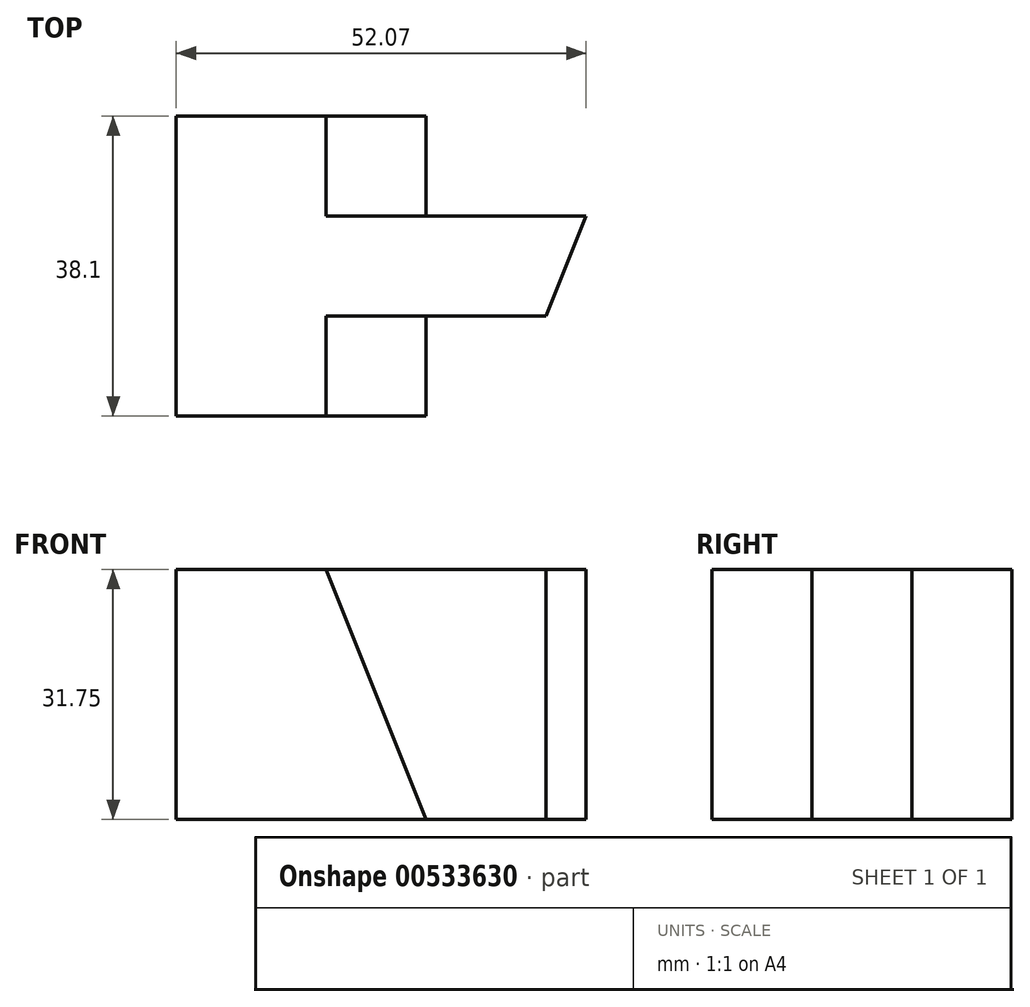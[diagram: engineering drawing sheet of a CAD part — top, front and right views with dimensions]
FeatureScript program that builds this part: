
annotation { "Feature Type Name" : "Feature", "Feature Type Description" : "" }
export const myFeature = defineFeature(function(context is Context, id is Id, definition is map)
    precondition{}
    {
        {
            var Q0;
            Q0=qCreatedBy(makeId("Front.planeOp"),FACE);
            var sketch = newSketch(context, id + "F0", { "sketchPlane" : qUnion([Q0])});
            skLineSegment(sketch, "E0", {"start": v(-43.55, 31.75) * mm, "end": v(-43.55, 0) * mm});
            skLineSegment(sketch, "E1", {"start": v(-43.55, 31.75) * mm, "end": v(-11.8, 31.75) * mm});
            skLineSegment(sketch, "E2", {"start": v(-11.8, 31.75) * mm, "end": v(-11.8, 0) * mm});
            skLineSegment(sketch, "E3", {"start": v(-11.8, 0) * mm, "end": v(-43.55, 0) * mm});
            skSolve(sketch);
        }
        {
            var Q0;
            Q0=makeQuery(id+"F0.imprint","IMPRINT",FACE,{"disambiguationData":[TD([[makeQuery(id+"F0.imprint","IMPRINT",EDGE,{"derivedFrom":sQuery(id+"F0.wireOp",EDGE,"E0")}),1.0]])]});
            extrude(context, id + "F1", {"entities" : qUnion([Q0]), "depth" : 38.1 * mm, "offsetDistance" : 25.4 * mm});
        }
        {
            var Q0;
            Q0=makeQuery(id+"F1.opExtrude","CAP_FACE",FACE,{"disambiguationData":[OSD([sQuery(id+"F0.wireOp",EDGE,"E0"),sQuery(id+"F0.wireOp",EDGE,"E1"),sQuery(id+"F0.wireOp",EDGE,"E2"),sQuery(id+"F0.wireOp",EDGE,"E3")])],"isStart":false});
            var sketch = newSketch(context, id + "F2", { "sketchPlane" : qUnion([Q0])});
            skLineSegment(sketch, "E4", {"start": v(-24.5, 31.75) * mm, "end": v(-11.8, 0) * mm});
            skSolve(sketch);
        }
        {
            var Q0;
            {var subQ0=sQuery(id+"F2.wireOp",EDGE,"E4");Q0=makeQuery(id+"F2.imprint","IMPRINT",FACE,{"disambiguationData":[TD([[makeQuery(id+"F2.imprint","IMPRINT",EDGE,{"derivedFrom":subQ0}),1.0]])]});}
            extrude(context, id + "F3", {"entities" : qUnion([Q0]), "operationType" : NewBodyOperationType.REMOVE, "oppositeDirection" : true, "depth" : 12.7 * mm, "offsetDistance" : 25.4 * mm});
        }
        {
            var Q0;
            Q0=makeQuery(id+"F1.opExtrude","CAP_FACE",FACE,{"disambiguationData":[OSD([sQuery(id+"F0.wireOp",EDGE,"E0"),sQuery(id+"F0.wireOp",EDGE,"E1"),sQuery(id+"F0.wireOp",EDGE,"E2"),sQuery(id+"F0.wireOp",EDGE,"E3")])],"isStart":true});
            var sketch = newSketch(context, id + "F4", { "sketchPlane" : qUnion([Q0])});
            skLineSegment(sketch, "E5", {"start": v(24.5, 31.75) * mm, "end": v(11.8, 0) * mm});
            skSolve(sketch);
        }
        {
            var Q0;
            {var subQ0=sQuery(id+"F4.wireOp",EDGE,"E5");Q0=makeQuery(id+"F4.imprint","IMPRINT",FACE,{"disambiguationData":[TD([[makeQuery(id+"F4.imprint","IMPRINT",EDGE,{"derivedFrom":subQ0}),-1.0]])]});}
            extrude(context, id + "F5", {"entities" : qUnion([Q0]), "operationType" : NewBodyOperationType.REMOVE, "oppositeDirection" : true, "depth" : 12.7 * mm, "offsetDistance" : 25.4 * mm});
        }
        {
            var Q0;
            Q0=makeQuery(id+"F1.opExtrude","SWEPT_FACE",FACE,{"disambiguationData":[OSD([sQuery(id+"F0.wireOp",EDGE,"E2")])]});
            extrude(context, id + "F6", {"entities" : qUnion([Q0]), "operationType" : NewBodyOperationType.ADD, "depth" : 25.4 * mm, "offsetDistance" : 25.4 * mm});
        }
        {
            var Q0;
            {var subQ0=sQuery(id+"F0.wireOp",EDGE,"E2");Q0=makeQuery(id+"F6.boolean.opBoolean","MERGE",FACE,{"derivedFrom":[makeQuery(id+"F3.boolean.opBoolean","COPY",FACE,{"derivedFrom":makeQuery(id+"F3.opExtrude","CAP_FACE",FACE,{"disambiguationData":[OSD([sQuery(id+"F0.wireOp",EDGE,"E1"),subQ0,sQuery(id+"F2.wireOp",EDGE,"E4")])],"isStart":false})}),makeQuery(id+"F6.opExtrude","SWEPT_FACE",FACE,{"disambiguationData":[OSD([subQ0]),TDD([makeQuery(id+"F3.boolean.opBoolean","COPY",EDGE,{"derivedFrom":makeQuery(id+"F3.opExtrude","CAP_EDGE",EDGE,{"disambiguationData":[OSD([subQ0])],"isStart":false})})])]})]});}
            var sketch = newSketch(context, id + "F7", { "sketchPlane" : qUnion([Q0])});
            skLineSegment(sketch, "E6", {"start": v(0.9, 31.75) * mm, "end": v(13.6, 0) * mm});
            skSolve(sketch);
        }
        {
            var Q0;
            {var subQ0=sQuery(id+"F7.wireOp",EDGE,"E6");Q0=makeQuery(id+"F7.imprint","IMPRINT",FACE,{"disambiguationData":[TD([[makeQuery(id+"F7.imprint","IMPRINT",EDGE,{"derivedFrom":subQ0}),1.0]])]});}
            extrude(context, id + "F8", {"entities" : qUnion([Q0]), "operationType" : NewBodyOperationType.REMOVE, "endBound" : BoundingType.THROUGH_ALL, "oppositeDirection" : true, "depth" : 25.4 * mm, "offsetDistance" : 25.4 * mm});
        }
    });
